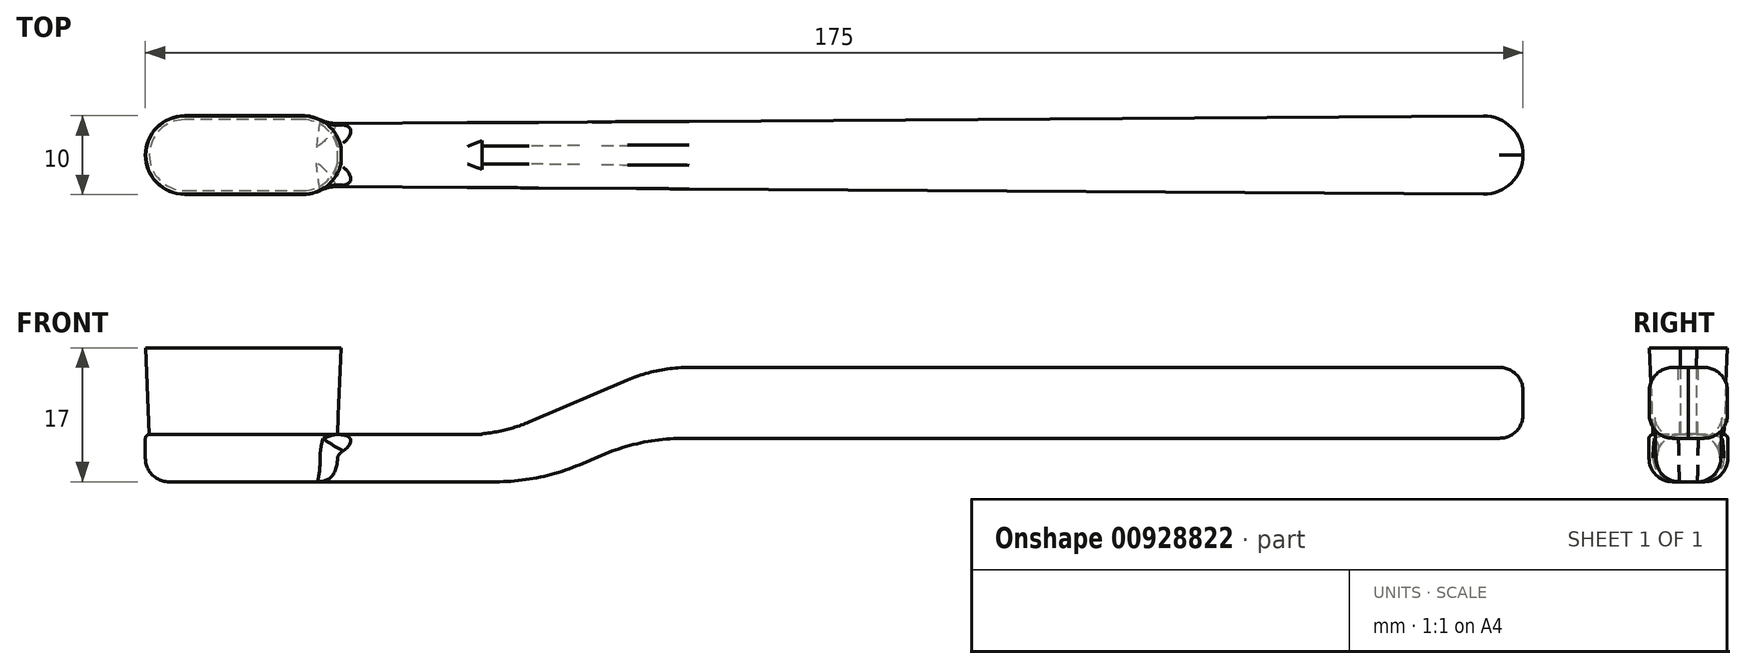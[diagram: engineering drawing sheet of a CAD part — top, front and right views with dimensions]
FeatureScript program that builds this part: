
annotation { "Feature Type Name" : "Feature", "Feature Type Description" : "" }
export const myFeature = defineFeature(function(context is Context, id is Id, definition is map)
    precondition{}
    {
        {
            var Q0;
            Q0=qCreatedBy(makeId("Front.planeOp"),FACE);
            var sketch = newSketch(context, id + "F0", { "sketchPlane" : qUnion([Q0])});
            skLineSegment(sketch, "E0", {"start": v(87.5, 0) * mm, "end": v(-87.5, 0) * mm, "construction": true});
            skLineSegment(sketch, "E1", {"start": v(-37.45, 0) * mm, "end": v(-24.48, 5.53) * mm});
            skLineSegment(sketch, "E2", {"start": v(-24.48, 5.53) * mm, "end": v(87.5, 5.53) * mm});
            skLineSegment(sketch, "E3", {"start": v(-37.45, 0) * mm, "end": v(-87.5, 0) * mm, "construction": true});
            skLineSegment(sketch, "E4", {"start": v(-87.5, 6) * mm, "end": v(-42.5, 6) * mm});
            skLineSegment(sketch, "E5", {"start": v(-42.5, 6) * mm, "end": v(-22.5, 14.53) * mm});
            skLineSegment(sketch, "E6", {"start": v(-22.5, 14.53) * mm, "end": v(87.5, 14.53) * mm});
            skLineSegment(sketch, "E7", {"start": v(87.5, 14.53) * mm, "end": v(87.5, 5.53) * mm});
            skLineSegment(sketch, "E8", {"start": v(-87.5, 6) * mm, "end": v(-87.5, 0) * mm});
            skLineSegment(sketch, "E9", {"start": v(-87.5, 0) * mm, "end": v(-37.45, 0) * mm});
            skSolve(sketch);
        }
        {
            var Q0;
            Q0 = qSketchRegion(id + "F0", true);
            extrude(context, id + "F1", {"entities" : qUnion([Q0]), "endBound" : BoundingType.SYMMETRIC, "depth" : 10 * mm, "offsetDistance" : 25 * mm});
        }
        {
            var Q0;
            Q0=qCreatedBy(makeId("Top.planeOp"),FACE);
            var sketch = newSketch(context, id + "F2", { "sketchPlane" : qUnion([Q0])});
            skLineSegment(sketch, "E10", {"start": v(-62.5, 6.97) * mm, "end": v(-62.5, 4) * mm});
            skLineSegment(sketch, "E11", {"start": v(-62.5, 4) * mm, "end": v(87.5, 5) * mm});
            skLineSegment(sketch, "E12", {"start": v(87.5, 5) * mm, "end": v(87.48, 7.74) * mm});
            skLineSegment(sketch, "E13", {"start": v(87.48, 7.74) * mm, "end": v(-62.5, 6.97) * mm});
            skLineSegment(sketch, "E14.MirrorCS", {"start": v(-62.5, -4) * mm, "end": v(87.5, -5) * mm});
            skLineSegment(sketch, "E15.MirrorCS", {"start": v(-62.5, -6.97) * mm, "end": v(-62.5, -4) * mm});
            skLineSegment(sketch, "E16.MirrorCS", {"start": v(87.48, -7.74) * mm, "end": v(-62.5, -6.97) * mm});
            skLineSegment(sketch, "E17.MirrorCS", {"start": v(87.5, -5) * mm, "end": v(87.48, -7.74) * mm});
            skSolve(sketch);
        }
        {
            var Q0;
            Q0 = qSketchRegion(id + "F2", true);
            extrude(context, id + "F3", {"entities" : qUnion([Q0]), "operationType" : NewBodyOperationType.REMOVE, "endBound" : BoundingType.SYMMETRIC, "oppositeDirection" : true, "depth" : 58.2 * mm, "offsetDistance" : 25 * mm});
        }
        {
            var Q0;
            Q0=makeQuery(id+"F3.boolean.opBoolean","MERGE",EDGE,{"derivedFrom":[makeQuery(id+"F1.opExtrude","CAP_EDGE",EDGE,{"disambiguationData":[OSD([sQuery(id+"F0.wireOp",EDGE,"E7")])],"isStart":false})],"fromTools":[makeQuery(id+"F3.opExtrude","SWEPT_EDGE",EDGE,{"disambiguationData":[OSD([sQuery(id+"F2.wireOp",EDGE,"E14.MirrorCS"),sQuery(id+"F2.wireOp",EDGE,"E17.MirrorCS")])]})]});
            var Q1;
            Q1=makeQuery(id+"F3.boolean.opBoolean","MERGE",EDGE,{"derivedFrom":[makeQuery(id+"F1.opExtrude","CAP_EDGE",EDGE,{"disambiguationData":[OSD([sQuery(id+"F0.wireOp",EDGE,"E7")])],"isStart":true})],"fromTools":[makeQuery(id+"F3.opExtrude","SWEPT_EDGE",EDGE,{"disambiguationData":[OSD([sQuery(id+"F2.wireOp",EDGE,"E11"),sQuery(id+"F2.wireOp",EDGE,"E12")])]})]});
            fillet(context, id + "F4", {"entities" : qUnion([Q0, Q1]), "radius" : 5 * mm, "tangentPropagation" : true, "allowEdgeOverflow" : false});
        }
        {
            var Q0;
            Q0=makeQuery(id+"F1.opExtrude","SWEPT_EDGE",EDGE,{"disambiguationData":[OSD([sQuery(id+"F0.wireOp",EDGE,"E5"),sQuery(id+"F0.wireOp",EDGE,"E6")])]});
            var Q1;
            Q1=makeQuery(id+"F1.opExtrude","SWEPT_EDGE",EDGE,{"disambiguationData":[OSD([sQuery(id+"F0.wireOp",EDGE,"E4"),sQuery(id+"F0.wireOp",EDGE,"E5")])]});
            fillet(context, id + "F5", {"entities" : qUnion([Q0, Q1]), "radius" : 20 * mm, "tangentPropagation" : true, "allowEdgeOverflow" : false});
        }
        {
            var Q0;
            Q0=makeQuery(id+"F1.opExtrude","SWEPT_EDGE",EDGE,{"disambiguationData":[OSD([sQuery(id+"F0.wireOp",EDGE,"E1"),sQuery(id+"F0.wireOp",EDGE,"E2")])]});
            var Q1;
            Q1=makeQuery(id+"F1.opExtrude","SWEPT_EDGE",EDGE,{"disambiguationData":[OSD([sQuery(id+"F0.wireOp",EDGE,"E1"),sQuery(id+"F0.wireOp",EDGE,"E9")])]});
            fillet(context, id + "F6", {"entities" : qUnion([Q0, Q1]), "radius" : 27 * mm, "tangentPropagation" : true, "allowEdgeOverflow" : false});
        }
        {
            var Q0;
            Q0=makeQuery(id+"F3.boolean.opBoolean","INTERSECT",EDGE,{"derivedFrom":[makeQuery(id+"F1.opExtrude","SWEPT_FACE",FACE,{"disambiguationData":[OSD([sQuery(id+"F0.wireOp",EDGE,"E6")])]}),makeQuery(id+"F3.opExtrude","SWEPT_FACE",FACE,{"disambiguationData":[OSD([sQuery(id+"F2.wireOp",EDGE,"E14.MirrorCS")])]})]});
            var Q1;
            Q1=makeQuery(id+"F3.boolean.opBoolean","INTERSECT",EDGE,{"derivedFrom":[makeQuery(id+"F1.opExtrude","SWEPT_FACE",FACE,{"disambiguationData":[OSD([sQuery(id+"F0.wireOp",EDGE,"E6")])]}),makeQuery(id+"F3.opExtrude","SWEPT_FACE",FACE,{"disambiguationData":[OSD([sQuery(id+"F2.wireOp",EDGE,"E11")])]})]});
            var Q2;
            Q2=makeQuery(id+"F4.opFillet","BLEND_EDGE",EDGE,{"blendedFrom":[makeQuery(id+"F3.boolean.opBoolean","MERGE",EDGE,{"derivedFrom":[makeQuery(id+"F1.opExtrude","CAP_EDGE",EDGE,{"disambiguationData":[OSD([sQuery(id+"F0.wireOp",EDGE,"E7")])],"isStart":false})],"fromTools":[makeQuery(id+"F3.opExtrude","SWEPT_EDGE",EDGE,{"disambiguationData":[OSD([sQuery(id+"F2.wireOp",EDGE,"E14.MirrorCS"),sQuery(id+"F2.wireOp",EDGE,"E17.MirrorCS")])]})]}),makeQuery(id+"F1.opExtrude","SWEPT_FACE",FACE,{"disambiguationData":[OSD([sQuery(id+"F0.wireOp",EDGE,"E6")])]})],"blendedInto":[makeQuery(id+"F1.opExtrude","SWEPT_FACE",FACE,{"disambiguationData":[OSD([sQuery(id+"F0.wireOp",EDGE,"E6")])]})]});
            var Q3;
            Q3=makeQuery(id+"F4.opFillet","BLEND_EDGE",EDGE,{"blendedFrom":[makeQuery(id+"F3.boolean.opBoolean","MERGE",EDGE,{"derivedFrom":[makeQuery(id+"F1.opExtrude","CAP_EDGE",EDGE,{"disambiguationData":[OSD([sQuery(id+"F0.wireOp",EDGE,"E7")])],"isStart":true})],"fromTools":[makeQuery(id+"F3.opExtrude","SWEPT_EDGE",EDGE,{"disambiguationData":[OSD([sQuery(id+"F2.wireOp",EDGE,"E11"),sQuery(id+"F2.wireOp",EDGE,"E12")])]})]}),makeQuery(id+"F1.opExtrude","SWEPT_FACE",FACE,{"disambiguationData":[OSD([sQuery(id+"F0.wireOp",EDGE,"E6")])]})],"blendedInto":[makeQuery(id+"F1.opExtrude","SWEPT_FACE",FACE,{"disambiguationData":[OSD([sQuery(id+"F0.wireOp",EDGE,"E6")])]})]});
            var Q4;
            Q4=makeQuery(id+"F4.opFillet","BLEND_EDGE",EDGE,{"blendedFrom":[makeQuery(id+"F3.boolean.opBoolean","MERGE",EDGE,{"derivedFrom":[makeQuery(id+"F1.opExtrude","CAP_EDGE",EDGE,{"disambiguationData":[OSD([sQuery(id+"F0.wireOp",EDGE,"E7")])],"isStart":true})],"fromTools":[makeQuery(id+"F3.opExtrude","SWEPT_EDGE",EDGE,{"disambiguationData":[OSD([sQuery(id+"F2.wireOp",EDGE,"E11"),sQuery(id+"F2.wireOp",EDGE,"E12")])]})]}),makeQuery(id+"F1.opExtrude","SWEPT_FACE",FACE,{"disambiguationData":[OSD([sQuery(id+"F0.wireOp",EDGE,"E2")])]})],"blendedInto":[makeQuery(id+"F1.opExtrude","SWEPT_FACE",FACE,{"disambiguationData":[OSD([sQuery(id+"F0.wireOp",EDGE,"E2")])]})]});
            var Q5;
            Q5=makeQuery(id+"F4.opFillet","BLEND_EDGE",EDGE,{"blendedFrom":[makeQuery(id+"F3.boolean.opBoolean","MERGE",EDGE,{"derivedFrom":[makeQuery(id+"F1.opExtrude","CAP_EDGE",EDGE,{"disambiguationData":[OSD([sQuery(id+"F0.wireOp",EDGE,"E7")])],"isStart":false})],"fromTools":[makeQuery(id+"F3.opExtrude","SWEPT_EDGE",EDGE,{"disambiguationData":[OSD([sQuery(id+"F2.wireOp",EDGE,"E14.MirrorCS"),sQuery(id+"F2.wireOp",EDGE,"E17.MirrorCS")])]})]}),makeQuery(id+"F1.opExtrude","SWEPT_FACE",FACE,{"disambiguationData":[OSD([sQuery(id+"F0.wireOp",EDGE,"E2")])]})],"blendedInto":[makeQuery(id+"F1.opExtrude","SWEPT_FACE",FACE,{"disambiguationData":[OSD([sQuery(id+"F0.wireOp",EDGE,"E2")])]})]});
            var Q6;
            Q6=makeQuery(id+"F3.boolean.opBoolean","INTERSECT",EDGE,{"derivedFrom":[makeQuery(id+"F1.opExtrude","SWEPT_FACE",FACE,{"disambiguationData":[OSD([sQuery(id+"F0.wireOp",EDGE,"E2")])]}),makeQuery(id+"F3.opExtrude","SWEPT_FACE",FACE,{"disambiguationData":[OSD([sQuery(id+"F2.wireOp",EDGE,"E14.MirrorCS")])]})]});
            var Q7;
            Q7=makeQuery(id+"F3.boolean.opBoolean","INTERSECT",EDGE,{"derivedFrom":[makeQuery(id+"F1.opExtrude","SWEPT_FACE",FACE,{"disambiguationData":[OSD([sQuery(id+"F0.wireOp",EDGE,"E1")])]}),makeQuery(id+"F3.opExtrude","SWEPT_FACE",FACE,{"disambiguationData":[OSD([sQuery(id+"F2.wireOp",EDGE,"E14.MirrorCS")])]})]});
            var Q8;
            Q8=makeQuery(id+"F3.boolean.opBoolean","INTERSECT",EDGE,{"derivedFrom":[makeQuery(id+"F1.opExtrude","SWEPT_FACE",FACE,{"disambiguationData":[OSD([sQuery(id+"F0.wireOp",EDGE,"E5")])]}),makeQuery(id+"F3.opExtrude","SWEPT_FACE",FACE,{"disambiguationData":[OSD([sQuery(id+"F2.wireOp",EDGE,"E14.MirrorCS")])]})]});
            var Q9;
            Q9=makeQuery(id+"F3.boolean.opBoolean","INTERSECT",EDGE,{"derivedFrom":[makeQuery(id+"F1.opExtrude","SWEPT_FACE",FACE,{"disambiguationData":[OSD([sQuery(id+"F0.wireOp",EDGE,"E5")])]}),makeQuery(id+"F3.opExtrude","SWEPT_FACE",FACE,{"disambiguationData":[OSD([sQuery(id+"F2.wireOp",EDGE,"E11")])]})]});
            var Q10;
            Q10=makeQuery(id+"F3.boolean.opBoolean","INTERSECT",EDGE,{"derivedFrom":[makeQuery(id+"F1.opExtrude","SWEPT_FACE",FACE,{"disambiguationData":[OSD([sQuery(id+"F0.wireOp",EDGE,"E1")])]}),makeQuery(id+"F3.opExtrude","SWEPT_FACE",FACE,{"disambiguationData":[OSD([sQuery(id+"F2.wireOp",EDGE,"E11")])]})]});
            var Q11;
            Q11=makeQuery(id+"F3.boolean.opBoolean","INTERSECT",EDGE,{"derivedFrom":[makeQuery(id+"F1.opExtrude","SWEPT_FACE",FACE,{"disambiguationData":[OSD([sQuery(id+"F0.wireOp",EDGE,"E4")])]}),makeQuery(id+"F3.opExtrude","SWEPT_FACE",FACE,{"disambiguationData":[OSD([sQuery(id+"F2.wireOp",EDGE,"E14.MirrorCS")])]})]});
            var Q12;
            Q12=makeQuery(id+"F3.boolean.opBoolean","INTERSECT",EDGE,{"derivedFrom":[makeQuery(id+"F1.opExtrude","SWEPT_FACE",FACE,{"disambiguationData":[OSD([sQuery(id+"F0.wireOp",EDGE,"E9")])]}),makeQuery(id+"F3.opExtrude","SWEPT_FACE",FACE,{"disambiguationData":[OSD([sQuery(id+"F2.wireOp",EDGE,"E14.MirrorCS")])]})]});
            var Q13;
            Q13=makeQuery(id+"F3.boolean.opBoolean","INTERSECT",EDGE,{"derivedFrom":[makeQuery(id+"F1.opExtrude","SWEPT_FACE",FACE,{"disambiguationData":[OSD([sQuery(id+"F0.wireOp",EDGE,"E4")])]}),makeQuery(id+"F3.opExtrude","SWEPT_FACE",FACE,{"disambiguationData":[OSD([sQuery(id+"F2.wireOp",EDGE,"E11")])]})]});
            var Q14;
            Q14=makeQuery(id+"F3.boolean.opBoolean","INTERSECT",EDGE,{"derivedFrom":[makeQuery(id+"F1.opExtrude","SWEPT_FACE",FACE,{"disambiguationData":[OSD([sQuery(id+"F0.wireOp",EDGE,"E9")])]}),makeQuery(id+"F3.opExtrude","SWEPT_FACE",FACE,{"disambiguationData":[OSD([sQuery(id+"F2.wireOp",EDGE,"E11")])]})]});
            var Q15;
            Q15=makeQuery(id+"F5.opFillet","BLEND_EDGE",EDGE,{"blendedFrom":[makeQuery(id+"F1.opExtrude","SWEPT_EDGE",EDGE,{"disambiguationData":[OSD([sQuery(id+"F0.wireOp",EDGE,"E4"),sQuery(id+"F0.wireOp",EDGE,"E5")])]}),makeQuery(id+"F3.boolean.opBoolean","COPY",FACE,{"derivedFrom":makeQuery(id+"F3.opExtrude","SWEPT_FACE",FACE,{"disambiguationData":[OSD([sQuery(id+"F2.wireOp",EDGE,"E14.MirrorCS")])]})})],"blendedInto":[makeQuery(id+"F3.boolean.opBoolean","COPY",FACE,{"derivedFrom":makeQuery(id+"F3.opExtrude","SWEPT_FACE",FACE,{"disambiguationData":[OSD([sQuery(id+"F2.wireOp",EDGE,"E14.MirrorCS")])]})})]});
            var Q16;
            Q16=makeQuery(id+"F5.opFillet","BLEND_EDGE",EDGE,{"blendedFrom":[makeQuery(id+"F1.opExtrude","SWEPT_EDGE",EDGE,{"disambiguationData":[OSD([sQuery(id+"F0.wireOp",EDGE,"E5"),sQuery(id+"F0.wireOp",EDGE,"E6")])]}),makeQuery(id+"F3.boolean.opBoolean","COPY",FACE,{"derivedFrom":makeQuery(id+"F3.opExtrude","SWEPT_FACE",FACE,{"disambiguationData":[OSD([sQuery(id+"F2.wireOp",EDGE,"E14.MirrorCS")])]})})],"blendedInto":[makeQuery(id+"F3.boolean.opBoolean","COPY",FACE,{"derivedFrom":makeQuery(id+"F3.opExtrude","SWEPT_FACE",FACE,{"disambiguationData":[OSD([sQuery(id+"F2.wireOp",EDGE,"E14.MirrorCS")])]})})]});
            var Q17;
            Q17=makeQuery(id+"F6.opFillet","BLEND_EDGE",EDGE,{"blendedFrom":[makeQuery(id+"F1.opExtrude","SWEPT_EDGE",EDGE,{"disambiguationData":[OSD([sQuery(id+"F0.wireOp",EDGE,"E1"),sQuery(id+"F0.wireOp",EDGE,"E2")])]}),makeQuery(id+"F3.boolean.opBoolean","COPY",FACE,{"derivedFrom":makeQuery(id+"F3.opExtrude","SWEPT_FACE",FACE,{"disambiguationData":[OSD([sQuery(id+"F2.wireOp",EDGE,"E14.MirrorCS")])]})})],"blendedInto":[makeQuery(id+"F3.boolean.opBoolean","COPY",FACE,{"derivedFrom":makeQuery(id+"F3.opExtrude","SWEPT_FACE",FACE,{"disambiguationData":[OSD([sQuery(id+"F2.wireOp",EDGE,"E14.MirrorCS")])]})})]});
            var Q18;
            Q18=makeQuery(id+"F6.opFillet","BLEND_EDGE",EDGE,{"blendedFrom":[makeQuery(id+"F1.opExtrude","SWEPT_EDGE",EDGE,{"disambiguationData":[OSD([sQuery(id+"F0.wireOp",EDGE,"E1"),sQuery(id+"F0.wireOp",EDGE,"E9")])]}),makeQuery(id+"F3.boolean.opBoolean","COPY",FACE,{"derivedFrom":makeQuery(id+"F3.opExtrude","SWEPT_FACE",FACE,{"disambiguationData":[OSD([sQuery(id+"F2.wireOp",EDGE,"E14.MirrorCS")])]})})],"blendedInto":[makeQuery(id+"F3.boolean.opBoolean","COPY",FACE,{"derivedFrom":makeQuery(id+"F3.opExtrude","SWEPT_FACE",FACE,{"disambiguationData":[OSD([sQuery(id+"F2.wireOp",EDGE,"E14.MirrorCS")])]})})]});
            var Q19;
            Q19=makeQuery(id+"F5.opFillet","BLEND_EDGE",EDGE,{"blendedFrom":[makeQuery(id+"F1.opExtrude","SWEPT_EDGE",EDGE,{"disambiguationData":[OSD([sQuery(id+"F0.wireOp",EDGE,"E4"),sQuery(id+"F0.wireOp",EDGE,"E5")])]}),makeQuery(id+"F3.boolean.opBoolean","COPY",FACE,{"derivedFrom":makeQuery(id+"F3.opExtrude","SWEPT_FACE",FACE,{"disambiguationData":[OSD([sQuery(id+"F2.wireOp",EDGE,"E11")])]})})],"blendedInto":[makeQuery(id+"F3.boolean.opBoolean","COPY",FACE,{"derivedFrom":makeQuery(id+"F3.opExtrude","SWEPT_FACE",FACE,{"disambiguationData":[OSD([sQuery(id+"F2.wireOp",EDGE,"E11")])]})})]});
            var Q20;
            Q20=makeQuery(id+"F6.opFillet","BLEND_EDGE",EDGE,{"blendedFrom":[makeQuery(id+"F1.opExtrude","SWEPT_EDGE",EDGE,{"disambiguationData":[OSD([sQuery(id+"F0.wireOp",EDGE,"E1"),sQuery(id+"F0.wireOp",EDGE,"E9")])]}),makeQuery(id+"F3.boolean.opBoolean","COPY",FACE,{"derivedFrom":makeQuery(id+"F3.opExtrude","SWEPT_FACE",FACE,{"disambiguationData":[OSD([sQuery(id+"F2.wireOp",EDGE,"E11")])]})})],"blendedInto":[makeQuery(id+"F3.boolean.opBoolean","COPY",FACE,{"derivedFrom":makeQuery(id+"F3.opExtrude","SWEPT_FACE",FACE,{"disambiguationData":[OSD([sQuery(id+"F2.wireOp",EDGE,"E11")])]})})]});
            fillet(context, id + "F7", {"entities" : qUnion([Q0, Q1, Q2, Q3, Q4, Q5, Q6, Q7, Q8, Q9, Q10, Q11, Q12, Q13, Q14, Q15, Q16, Q17, Q18, Q19, Q20]), "radius" : 3 * mm, "tangentPropagation" : true, "allowEdgeOverflow" : false});
        }
        {
            var Q0;
            Q0=makeQuery(id+"F3.boolean.opBoolean","INTERSECT",EDGE,{"derivedFrom":[makeQuery(id+"F1.opExtrude","CAP_FACE",FACE,{"disambiguationData":[OSD([sQuery(id+"F0.wireOp",EDGE,"E1"),sQuery(id+"F0.wireOp",EDGE,"E2"),sQuery(id+"F0.wireOp",EDGE,"E4"),sQuery(id+"F0.wireOp",EDGE,"E5"),sQuery(id+"F0.wireOp",EDGE,"E6"),sQuery(id+"F0.wireOp",EDGE,"E7"),sQuery(id+"F0.wireOp",EDGE,"E8"),sQuery(id+"F0.wireOp",EDGE,"E9")])],"isStart":false}),makeQuery(id+"F3.opExtrude","SWEPT_FACE",FACE,{"disambiguationData":[OSD([sQuery(id+"F2.wireOp",EDGE,"E15.MirrorCS")])]})]});
            var Q1;
            Q1=makeQuery(id+"F3.boolean.opBoolean","INTERSECT",EDGE,{"derivedFrom":[makeQuery(id+"F1.opExtrude","CAP_FACE",FACE,{"disambiguationData":[OSD([sQuery(id+"F0.wireOp",EDGE,"E1"),sQuery(id+"F0.wireOp",EDGE,"E2"),sQuery(id+"F0.wireOp",EDGE,"E4"),sQuery(id+"F0.wireOp",EDGE,"E5"),sQuery(id+"F0.wireOp",EDGE,"E6"),sQuery(id+"F0.wireOp",EDGE,"E7"),sQuery(id+"F0.wireOp",EDGE,"E8"),sQuery(id+"F0.wireOp",EDGE,"E9")])],"isStart":true}),makeQuery(id+"F3.opExtrude","SWEPT_FACE",FACE,{"disambiguationData":[OSD([sQuery(id+"F2.wireOp",EDGE,"E10")])]})]});
            fillet(context, id + "F8", {"entities" : qUnion([Q0, Q1]), "radius" : 5 * mm, "tangentPropagation" : true, "allowEdgeOverflow" : false});
        }
        {
            var Q0;
            Q0=makeQuery(id+"F1.opExtrude","CAP_EDGE",EDGE,{"disambiguationData":[OSD([sQuery(id+"F0.wireOp",EDGE,"E8")])],"isStart":true});
            var Q1;
            Q1=makeQuery(id+"F1.opExtrude","CAP_EDGE",EDGE,{"disambiguationData":[OSD([sQuery(id+"F0.wireOp",EDGE,"E8")])],"isStart":false});
            fillet(context, id + "F9", {"entities" : qUnion([Q0, Q1]), "radius" : 5 * mm, "tangentPropagation" : true, "allowEdgeOverflow" : false});
        }
        {
            var Q0;
            {var subQ0=sQuery(id+"F0.wireOp",EDGE,"E4");Q0=makeQuery(id+"F8.opFillet","BLEND_EDGE",EDGE,{"blendedFrom":[makeQuery(id+"F3.boolean.opBoolean","INTERSECT",EDGE,{"derivedFrom":[makeQuery(id+"F1.opExtrude","CAP_FACE",FACE,{"disambiguationData":[OSD([sQuery(id+"F0.wireOp",EDGE,"E1"),sQuery(id+"F0.wireOp",EDGE,"E2"),subQ0,sQuery(id+"F0.wireOp",EDGE,"E5"),sQuery(id+"F0.wireOp",EDGE,"E6"),sQuery(id+"F0.wireOp",EDGE,"E7"),sQuery(id+"F0.wireOp",EDGE,"E8"),sQuery(id+"F0.wireOp",EDGE,"E9")])],"isStart":false}),makeQuery(id+"F3.opExtrude","SWEPT_FACE",FACE,{"disambiguationData":[OSD([sQuery(id+"F2.wireOp",EDGE,"E15.MirrorCS")])]})]}),makeQuery(id+"F1.opExtrude","SWEPT_FACE",FACE,{"disambiguationData":[OSD([subQ0])]})],"blendedInto":[makeQuery(id+"F1.opExtrude","SWEPT_FACE",FACE,{"disambiguationData":[OSD([subQ0])]})]});}
            fillet(context, id + "F10", {"entities" : qUnion([Q0]), "radius" : 0.5 * mm, "tangentPropagation" : true, "allowEdgeOverflow" : false});
        }
        {
            var Q0;
            Q0=makeQuery(id+"F1.opExtrude","CAP_EDGE",EDGE,{"disambiguationData":[OSD([sQuery(id+"F0.wireOp",EDGE,"E9")])],"isStart":false});
            fillet(context, id + "F11", {"entities" : qUnion([Q0]), "radius" : 3 * mm, "tangentPropagation" : true, "allowEdgeOverflow" : false});
        }
        {
            var Q0;
            {var subQ0=sQuery(id+"F0.wireOp",EDGE,"E4");Q0=makeQuery(id+"F8.opFillet","BLEND_EDGE",EDGE,{"blendedFrom":[makeQuery(id+"F3.boolean.opBoolean","INTERSECT",EDGE,{"derivedFrom":[makeQuery(id+"F1.opExtrude","CAP_FACE",FACE,{"disambiguationData":[OSD([sQuery(id+"F0.wireOp",EDGE,"E1"),sQuery(id+"F0.wireOp",EDGE,"E2"),subQ0,sQuery(id+"F0.wireOp",EDGE,"E5"),sQuery(id+"F0.wireOp",EDGE,"E6"),sQuery(id+"F0.wireOp",EDGE,"E7"),sQuery(id+"F0.wireOp",EDGE,"E8"),sQuery(id+"F0.wireOp",EDGE,"E9")])],"isStart":false}),makeQuery(id+"F3.opExtrude","SWEPT_FACE",FACE,{"disambiguationData":[OSD([sQuery(id+"F2.wireOp",EDGE,"E15.MirrorCS")])]})]}),makeQuery(id+"F7.opFillet","BLEND_FACE",FACE,{"disambiguationData":[OSD([subQ0,sQuery(id+"F2.wireOp",EDGE,"E14.MirrorCS")])]})],"blendedInto":[makeQuery(id+"F7.opFillet","BLEND_FACE",FACE,{"disambiguationData":[OSD([subQ0,sQuery(id+"F2.wireOp",EDGE,"E14.MirrorCS")])]})]});}
            var Q1;
            {var subQ0=sQuery(id+"F0.wireOp",EDGE,"E4");Q1=makeQuery(id+"F8.opFillet","BLEND_EDGE",EDGE,{"blendedFrom":[makeQuery(id+"F3.boolean.opBoolean","INTERSECT",EDGE,{"derivedFrom":[makeQuery(id+"F1.opExtrude","CAP_FACE",FACE,{"disambiguationData":[OSD([sQuery(id+"F0.wireOp",EDGE,"E1"),sQuery(id+"F0.wireOp",EDGE,"E2"),subQ0,sQuery(id+"F0.wireOp",EDGE,"E5"),sQuery(id+"F0.wireOp",EDGE,"E6"),sQuery(id+"F0.wireOp",EDGE,"E7"),sQuery(id+"F0.wireOp",EDGE,"E8"),sQuery(id+"F0.wireOp",EDGE,"E9")])],"isStart":true}),makeQuery(id+"F3.opExtrude","SWEPT_FACE",FACE,{"disambiguationData":[OSD([sQuery(id+"F2.wireOp",EDGE,"E10")])]})]}),makeQuery(id+"F7.opFillet","BLEND_FACE",FACE,{"disambiguationData":[OSD([subQ0,sQuery(id+"F2.wireOp",EDGE,"E11")])]})],"blendedInto":[makeQuery(id+"F7.opFillet","BLEND_FACE",FACE,{"disambiguationData":[OSD([subQ0,sQuery(id+"F2.wireOp",EDGE,"E11")])]})]});}
            fillet(context, id + "F12", {"entities" : qUnion([Q0, Q1]), "radius" : 5 * mm, "tangentPropagation" : true, "allowEdgeOverflow" : false});
        }
        {
            var Q0;
            Q0=qCreatedBy(makeId("Front.planeOp"),FACE);
            var sketch = newSketch(context, id + "F13", { "sketchPlane" : qUnion([Q0])});
            skLineSegment(sketch, "E18", {"start": v(-88.94, 17) * mm, "end": v(-87, 6) * mm});
            skLineSegment(sketch, "E19", {"start": v(-87, 6) * mm, "end": v(-63, 6) * mm});
            skLineSegment(sketch, "E20", {"start": v(-63, 6) * mm, "end": v(-61.06, 17) * mm});
            skLineSegment(sketch, "E21", {"start": v(-61.06, 17) * mm, "end": v(-88.94, 17) * mm});
            skLineSegment(sketch, "E22", {"start": v(-75, 6) * mm, "end": v(-75, 17) * mm});
            skSolve(sketch);
        }
        {
            var Q0;
            {var subQ0=sQuery(id+"F13.wireOp",EDGE,"E20");Q0=makeQuery(id+"F13.imprint","IMPRINT",FACE,{"disambiguationData":[TD([[makeQuery(id+"F13.imprint","IMPRINT",EDGE,{"derivedFrom":subQ0}),1.0]])]});}
            var Q1;
            {var subQ0=sQuery(id+"F13.wireOp",EDGE,"E18");Q1=makeQuery(id+"F13.imprint","IMPRINT",FACE,{"disambiguationData":[TD([[makeQuery(id+"F13.imprint","IMPRINT",EDGE,{"derivedFrom":subQ0}),1.0]])]});}
            extrude(context, id + "F14", {"entities" : qUnion([Q0, Q1]), "endBound" : BoundingType.SYMMETRIC, "depth" : 10 * mm, "offsetDistance" : 25 * mm});
        }
        {
            var Q0;
            Q0=makeQuery(id+"F1.opExtrude","SWEPT_FACE",FACE,{"disambiguationData":[OSD([sQuery(id+"F0.wireOp",EDGE,"E4")])]});
            var sketch = newSketch(context, id + "F15", { "sketchPlane" : qUnion([Q0])});
            skArc(sketch, "E23.0", {"start": v(-63.11, 1) * mm, "mid": v(-64.7, 3.52) * mm, "end": v(-67.5, 4.5) * mm});
            skLineSegment(sketch, "E23.1", {"start": v(-67.5, 4.5) * mm, "end": v(-82.5, 4.5) * mm});
            skArc(sketch, "E23.2", {"start": v(-82.5, 4.5) * mm, "mid": v(-87, 0) * mm, "end": v(-82.5, -4.5) * mm});
            skLineSegment(sketch, "E23.3", {"start": v(-82.5, -4.5) * mm, "end": v(-67.5, -4.5) * mm});
            skArc(sketch, "E23.4", {"start": v(-67.5, -4.5) * mm, "mid": v(-64.7, -3.52) * mm, "end": v(-63.11, -1) * mm});
            skLineSegment(sketch, "E24", {"start": v(-63.11, -1) * mm, "end": v(-63.11, 1) * mm});
            skLineSegment(sketch, "E25.bottom", {"start": v(-99.37, 9.28) * mm, "end": v(-44.74, 9.28) * mm});
            skLineSegment(sketch, "E25.top", {"start": v(-99.37, -7.7) * mm, "end": v(-44.74, -7.7) * mm});
            skLineSegment(sketch, "E25.left", {"start": v(-99.37, 9.28) * mm, "end": v(-99.37, -7.7) * mm});
            skLineSegment(sketch, "E25.right", {"start": v(-44.74, 9.28) * mm, "end": v(-44.74, -7.7) * mm});
            skSolve(sketch);
        }
        {
            var Q0;
            {var subQ0=sQuery(id+"F15.wireOp",EDGE,"E24");Q0=makeQuery(id+"F15.imprint","IMPRINT",FACE,{"disambiguationData":[TD([[makeQuery(id+"F15.imprint","IMPRINT",EDGE,{"derivedFrom":subQ0}),-1.0]])]});}
            var Q1;
            {var subQ10=sQuery(id+"F15.wireOp",EDGE,"E23.0");Q1=makeQuery(id+"F15.imprint","IMPRINT",FACE,{"disambiguationData":[TD([[makeQuery(id+"F15.imprint","IMPRINT",EDGE,{"derivedFrom":subQ10}),-1.0]])]});}
            extrude(context, id + "F16", {"entities" : qUnion([Q0, Q1]), "operationType" : NewBodyOperationType.REMOVE, "depth" : 22.1 * mm, "offsetDistance" : 25 * mm, "hasDraft" : true, "draftAngle" : 2.4 * degree, "draftPullDirection" : true});
        }
    });
